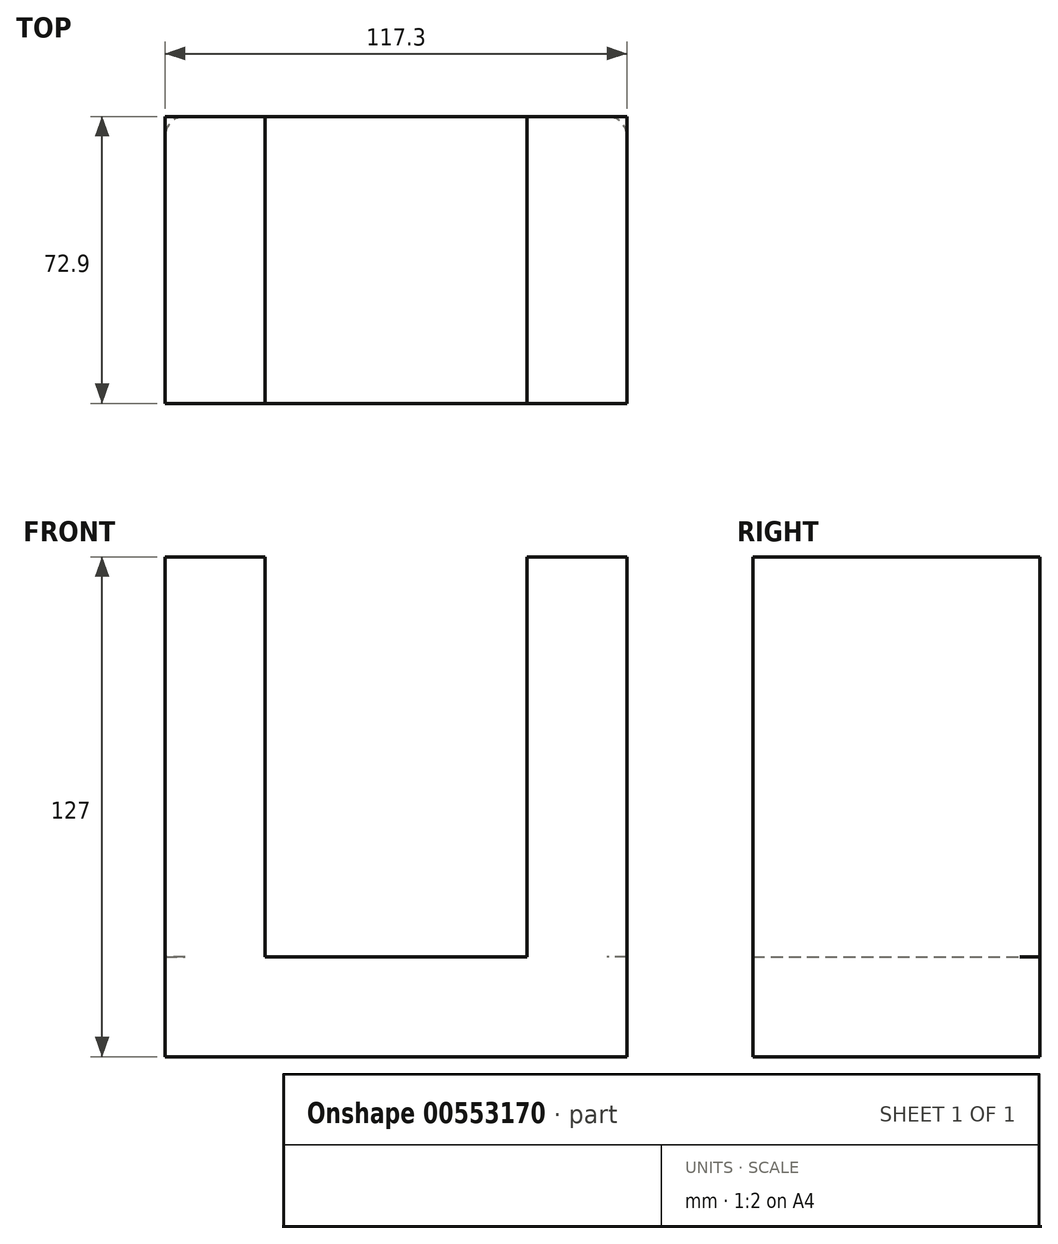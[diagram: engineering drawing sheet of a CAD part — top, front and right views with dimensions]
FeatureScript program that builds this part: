
annotation { "Feature Type Name" : "Feature", "Feature Type Description" : "" }
export const myFeature = defineFeature(function(context is Context, id is Id, definition is map)
    precondition{}
    {
        {
            var Q0;
            Q0=qCreatedBy(makeId("Top.planeOp"),FACE);
            var sketch = newSketch(context, id + "F0", { "sketchPlane" : qUnion([Q0])});
            skLineSegment(sketch, "E0.bottom", {"start": v(58.65, 36.45) * mm, "end": v(-58.65, 36.45) * mm});
            skLineSegment(sketch, "E0.top", {"start": v(58.65, -36.45) * mm, "end": v(-58.65, -36.45) * mm});
            skLineSegment(sketch, "E0.left", {"start": v(58.65, 36.45) * mm, "end": v(58.65, -36.45) * mm});
            skLineSegment(sketch, "E0.right", {"start": v(-58.65, 36.45) * mm, "end": v(-58.65, -36.45) * mm});
            skPoint(sketch, "E0.middle", {"position": v(0, 0) * mm});
            skSolve(sketch);
        }
        {
            var Q0;
            Q0 = qSketchRegion(id + "F0", true);
            extrude(context, id + "F1", {"entities" : qUnion([Q0]), "depth" : 25.4 * mm, "offsetDistance" : 25.4 * mm});
        }
        {
            var Q0;
            Q0=makeQuery(id+"F1.opExtrude","SWEPT_EDGE",EDGE,{"disambiguationData":[OSD([sQuery(id+"F0.wireOp",EDGE,"E0.bottom"),sQuery(id+"F0.wireOp",EDGE,"E0.left")])]});
            fillet(context, id + "F2", {"entities" : qUnion([Q0]), "radius" : 5.08 * mm, "tangentPropagation" : true, "allowEdgeOverflow" : false});
        }
        {
            var Q0;
            Q0=makeQuery(id+"F1.opExtrude","SWEPT_EDGE",EDGE,{"disambiguationData":[OSD([sQuery(id+"F0.wireOp",EDGE,"E0.bottom"),sQuery(id+"F0.wireOp",EDGE,"E0.right")])]});
            fillet(context, id + "F3", {"entities" : qUnion([Q0]), "radius" : 5.08 * mm, "tangentPropagation" : true, "allowEdgeOverflow" : false});
        }
        {
            var Q0;
            Q0=makeQuery(id+"F1.opExtrude","CAP_FACE",FACE,{"disambiguationData":[OSD([sQuery(id+"F0.wireOp",EDGE,"E0.bottom"),sQuery(id+"F0.wireOp",EDGE,"E0.top"),sQuery(id+"F0.wireOp",EDGE,"E0.left"),sQuery(id+"F0.wireOp",EDGE,"E0.right")])],"isStart":false});
            var sketch = newSketch(context, id + "F4", { "sketchPlane" : qUnion([Q0])});
            skLineSegment(sketch, "E1.bottom", {"start": v(-58.65, -36.45) * mm, "end": v(-33.25, -36.45) * mm});
            skLineSegment(sketch, "E1.top", {"start": v(-58.65, 36.45) * mm, "end": v(-33.25, 36.45) * mm});
            skLineSegment(sketch, "E1.left", {"start": v(-58.65, -36.45) * mm, "end": v(-58.65, 36.45) * mm});
            skLineSegment(sketch, "E1.right", {"start": v(-33.25, -36.45) * mm, "end": v(-33.25, 36.45) * mm});
            skLineSegment(sketch, "E2.bottom", {"start": v(58.65, -36.45) * mm, "end": v(33.25, -36.45) * mm});
            skLineSegment(sketch, "E2.top", {"start": v(58.65, 36.45) * mm, "end": v(33.25, 36.45) * mm});
            skLineSegment(sketch, "E2.left", {"start": v(58.65, -36.45) * mm, "end": v(58.65, 36.45) * mm});
            skLineSegment(sketch, "E2.right", {"start": v(33.25, -36.45) * mm, "end": v(33.25, 36.45) * mm});
            skSolve(sketch);
        }
        {
            var Q0;
            Q0 = qSketchRegion(id + "F4", true);
            extrude(context, id + "F5", {"entities" : qUnion([Q0]), "operationType" : NewBodyOperationType.ADD, "depth" : 101.6 * mm, "offsetDistance" : 25.4 * mm});
        }
    });
